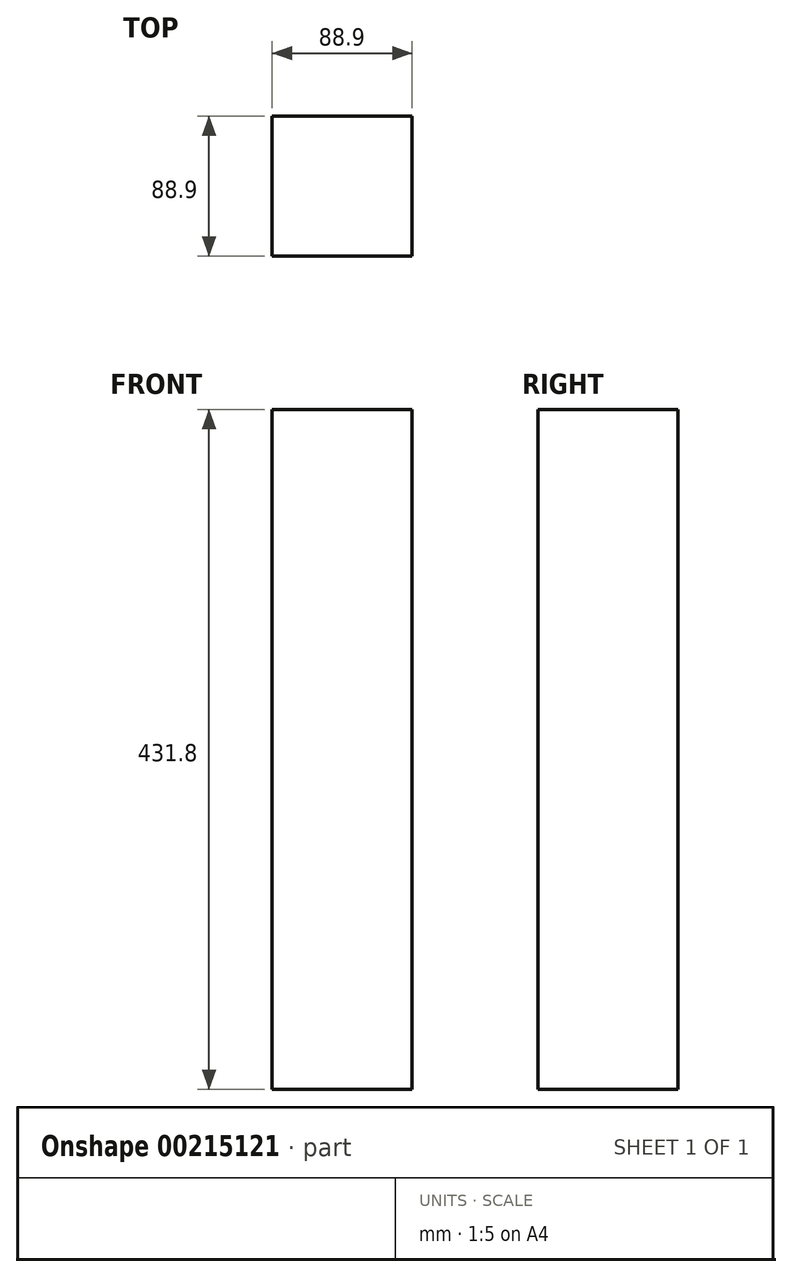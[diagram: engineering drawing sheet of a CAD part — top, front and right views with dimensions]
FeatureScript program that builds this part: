
annotation { "Feature Type Name" : "Feature", "Feature Type Description" : "" }
export const myFeature = defineFeature(function(context is Context, id is Id, definition is map)
    precondition{}
    {
        {
            var Q0;
            Q0=qCreatedBy(makeId("Top.planeOp"),FACE);
            var sketch = newSketch(context, id + "F0", { "sketchPlane" : qUnion([Q0])});
            skLineSegment(sketch, "E0.bottom", {"start": v(0, 0) * mm, "end": v(88.9, 0) * mm});
            skLineSegment(sketch, "E0.top", {"start": v(0, 88.9) * mm, "end": v(88.9, 88.9) * mm});
            skLineSegment(sketch, "E0.left", {"start": v(0, 0) * mm, "end": v(0, 88.9) * mm});
            skLineSegment(sketch, "E0.right", {"start": v(88.9, 0) * mm, "end": v(88.9, 88.9) * mm});
            skSolve(sketch);
        }
        {
            var Q0;
            Q0 = qSketchRegion(id + "F0", true);
            extrude(context, id + "F1", {"entities" : qUnion([Q0]), "depth" : 431.8 * mm, "offsetDistance" : 25.4 * mm});
        }
    });
